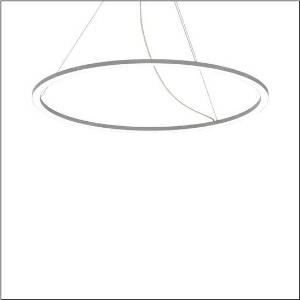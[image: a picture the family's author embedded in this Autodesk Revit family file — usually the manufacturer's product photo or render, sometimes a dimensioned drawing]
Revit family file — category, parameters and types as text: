
# Revit family: silica_21_ring-d_5pjbd4d3204a
name_source: partatom
category: Lighting Fixtures
units: mm (PartAtom-declared; Revit-internal decimal feet)

## family parameters
Cut with Voids When Loaded = No
Host = Face
Light Source = No
Part Type = Normal
Room Calculation Point = No
Round Connector Dimension = Use Diameter
Shared = No

## types (1)
- Silica 21 Ring-D (1 x LED, 11350 lm, 125 W, 4000K)
    Apparent Load = 125 VA
    CIE Flux Codes = 37 69 92 100 100
    Color Rendering = 80
    Color Temperature = 4000K
    Default Elevation = 1800 mm
    Description = Silica 21 Ring-D, suspended luminaire, of PMMA, frosted, light emission: ring underside luminous distribution, primary light characteristic: symmetric, installation type: suspended mounting, LED, rated luminous flux: 11.350lm, luminous efficacy: 91lm/W, light colour: 840, colour temperature: 4000K, control gear: DALI 2, with terminal, 5-pole, mains connection: 230V, AC/DC, 0/50..60Hz, rated input power: 125W, housing, of extruded aluminium section, metallic grey (RAL 9006), diameter: 1.450mm, ceiling canopy, metallic grey (RAL 9006), protection rating (lamp compartment): IP40, insulation class (complete): insulation class I (protective earthing), certification: CE, impact resistance: IK02, permissible operating ambient temperature: 0..+35°C, packaging unit: 1 piece
    Height = 25 mm  [stored 0.082021 ft]
    Lamp = 1 x LED
    Lamp Light Flux = 11350 lm
    Lamp Power = 125 W
    Lamp count = 1
    Length = 1450 mm
    Luminous efficacy = 91 lm/W
    Manufacturer = Siteco
    ModVariant = No
    Model = 5PJBD4D3204A
    Mounting Place = Ceiling
    Mounting Type = Pendant
    Number of Poles = 1
    OnlyDefault = Yes
    Power Factor = 1
    Product Name = Silica 21 Ring-D
    Product group = suspended luminaire
    ProductGroupID = 904
    Protection Class = Protection class I
    Protection Degree = IP 40
    RLX_Detail_Level = 1
    RLX_Emergency_Light_Flux = 0 lm
    RLX_Emergency_Type = 0
    RLX_Emergency_Type_DB = No
    RlxData = <blob elided: 17921 chars, md5=3a9bce29>
    Socket = socket
    Standby Power = 0 W
    System Light Flux = 11350 lm
    System Power = 125 W
    Type Comments = Product without accessories
    Type Image = l_1251748.jpg
    URL = http://relux.com
    VarID = ---
    Voltage = 0 V
    Weight = 0.00 kg
    Width = 0 mm  [stored 0 ft]

note: [stored X ft] marks values corroborated as IEEE doubles in the binary element streams (Revit-internal decimal feet)

## geometry (parser evidence)
native form markers: Blend x4, Sweep x11
no freeform markers — native parametric forms only
